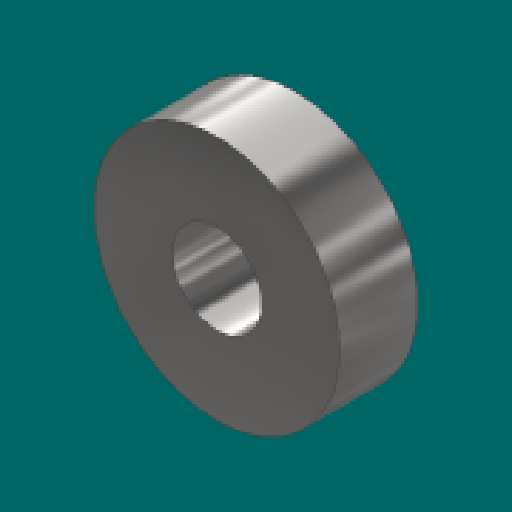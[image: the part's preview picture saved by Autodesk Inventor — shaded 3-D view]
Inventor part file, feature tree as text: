
AUTODESK INVENTOR PART (.ipt)
format: ipt  version: 2023.1 (Build 271208000, 208)  size: 101,376 bytes
history: native  units: in
note: dims shown in document units (in); Inventor stores cm internally (conversion verified against a paired STEP export)
features: extrude x1, sketch x1
ambient origin geometry x8: Origin, YZ Plane, XZ Plane, XY Plane, X Axis, Y Axis, Z Axis, Center Point
bodies: Solid1 (feature_tree)
feature tree (2):
  extrude  "Extrusion1"  Depth=0.2756in
  sketch  "Sketch1"  dims[d0=0.315in d1=0.8661in d2=0.2756in d3=0.0in]
